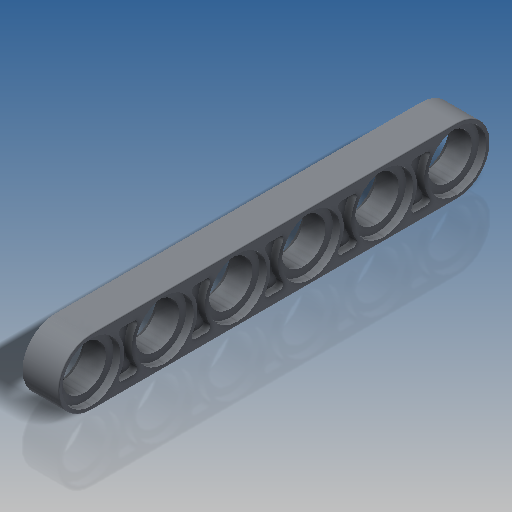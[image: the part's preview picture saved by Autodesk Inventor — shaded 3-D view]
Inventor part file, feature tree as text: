
AUTODESK INVENTOR PART (.ipt)
format: ipt  version: 2018.3 (Build 223284000, 284)  size: 384,512 bytes
history: native  units: mm
features: extrude x3, sketch x2, mirror x1, fillet x1
ambient origin geometry x8: Origin, YZ Plane, XZ Plane, XY Plane, X Axis, Y Axis, Z Axis, Center Point
bodies: Solid1 (feature_tree)
feature tree (7):
  extrude  "Extrusion4"  Depth=7.2mm
  sketch  "Sketch11"  dims[d56=0.1mm d59=6.4mm d60=4.8mm d61=6.4mm d62=0.8mm d63=0.0mm d64=8.0mm d65=45.0deg d66=50.0mm d68=8.0mm d69=10.0mm d71=10.0mm d73=0.8mm d74=0.0mm d75=0.4mm]
  extrude  "Extrusion16"  Depth=0.4mm
  extrude  "Extrusion17"  Depth=0.4mm
  mirror  "Mirror3"
  fillet  "Fillet1"  Radius=6.4mm
  sketch  "Sketch3"  dims[d15=4.0mm d16=0.0mm d49=7.2mm]
